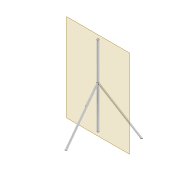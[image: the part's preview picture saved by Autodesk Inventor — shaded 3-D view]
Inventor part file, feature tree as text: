
AUTODESK INVENTOR PART (.ipt)
format: ipt  version: 2022 (Build 260153000, 153)  size: 95,232 bytes
history: native  units: mm
features: sketch x3, extrude x1, plane x1, loft x1, pattern_circular x1, projected_geometry x1
ambient origin geometry x8: Origin, YZ Plane, XZ Plane, XY Plane, X Axis, Y Axis, Z Axis, Center Point
bodies: Solid1 (feature_tree)
feature tree (8):
  extrude  "Extrusion1"  Depth=1500.0mm TaperAngle=0.0deg
  plane  "Work Plane1"
  loft  "Loft1"
  pattern_circular  "Circular Pattern1"  Count=60  [1 undecoded]
  sketch  "Sketch1"  dims[d0=34.5mm d1=1500.0mm d2=0.0mm]
  sketch  "Sketch2"  dims[d3=-800.0mm d4=34.5mm d5=600.0mm]
  projected_geometry  "Projected Loop1"
  sketch  "Sketch3"  dims[d6=0.0mm d7=90.0deg d8=0.0mm d9=90.0deg d10=30.0mm d11=360.0deg]
note: 1 required parameter value undecoded (feature->parameter linkage not recoverable at this tier; creation-order binding heuristic only, values carry confidence <= 0.55)
